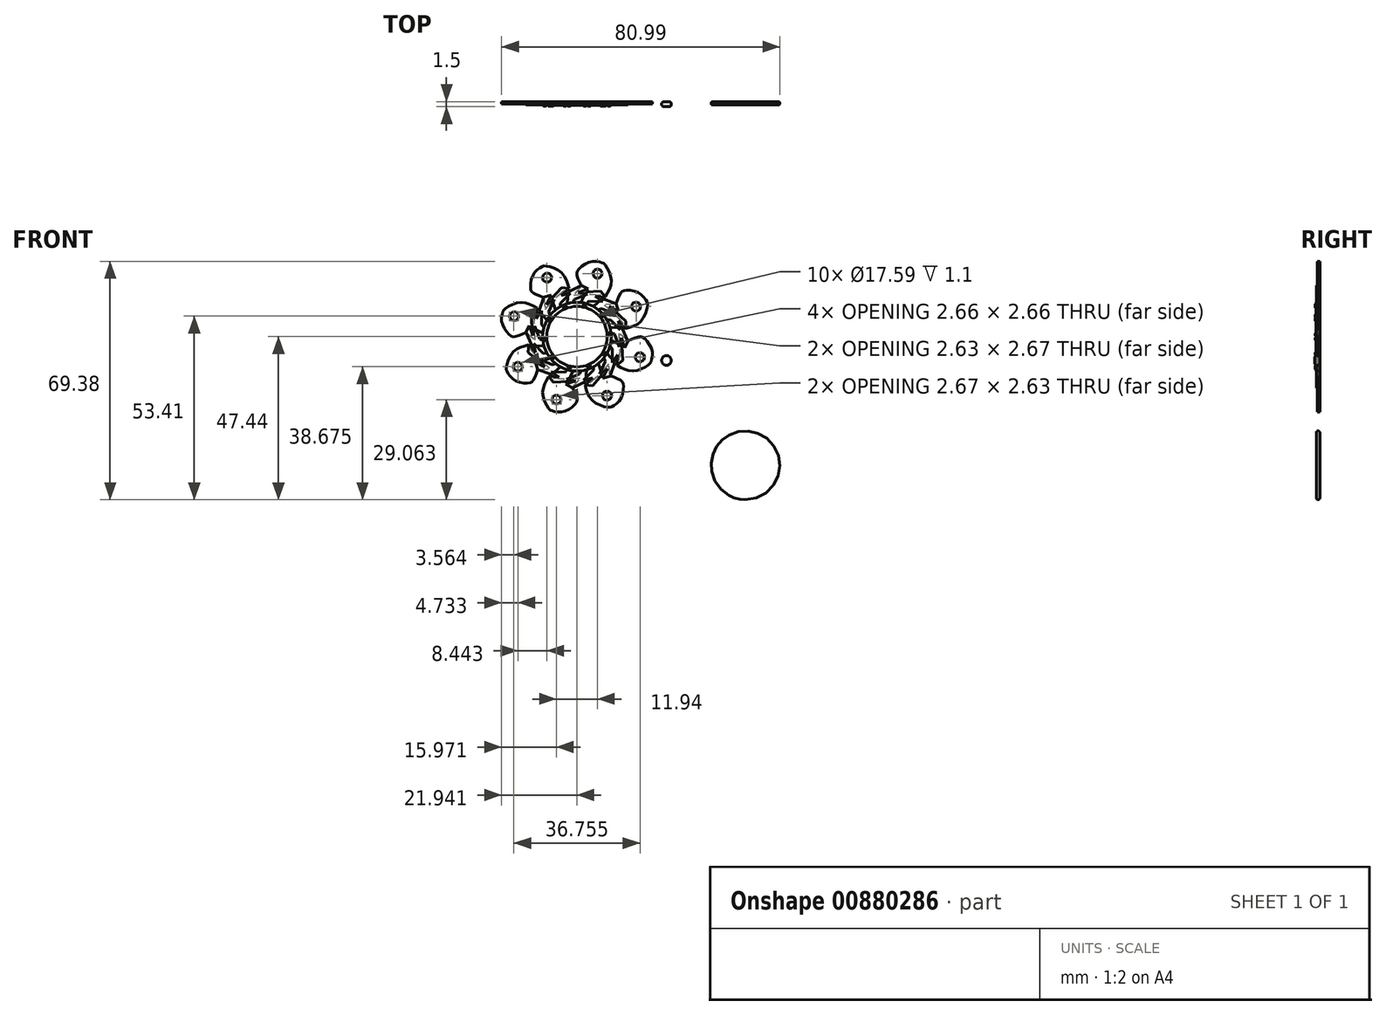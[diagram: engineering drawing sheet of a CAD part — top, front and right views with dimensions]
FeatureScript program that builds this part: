
annotation { "Feature Type Name" : "Feature", "Feature Type Description" : "" }
export const myFeature = defineFeature(function(context is Context, id is Id, definition is map)
    precondition{}
    {
        {
            var Q0;
            Q0=qCreatedBy(makeId("Front.planeOp"),FACE);
            var sketch = newSketch(context, id + "F0", { "sketchPlane" : qUnion([Q0])});
            skCircle(sketch, "E0", {"center": v(0, 0) * mm, "radius": 10 * mm});
            skSolve(sketch);
        }
        {
            var Q0;
            Q0=makeQuery(id+"F0.imprint","IMPRINT",FACE,{"disambiguationData":[TD([[makeQuery(id+"F0.imprint","IMPRINT",EDGE,{"derivedFrom":sQuery(id+"F0.wireOp",EDGE,"E0")}),1.0]])]});
            extrude(context, id + "F1", {"entities" : qUnion([Q0]), "depth" : 1 * mm, "offsetDistance" : 25 * mm});
        }
        {
            var Q0;
            Q0=makeQuery(id+"F1.opExtrude","CAP_FACE",FACE,{"disambiguationData":[OSD([sQuery(id+"F0.wireOp",EDGE,"E0")])],"isStart":false});
            var Q1;
            Q1=makeQuery(id+"F1.opExtrude","CAP_FACE",FACE,{"disambiguationData":[OSD([sQuery(id+"F0.wireOp",EDGE,"E0")])],"isStart":true});
            fillet(context, id + "F2", {"entities" : qUnion([Q0, Q1]), "radius" : .5 * mm, "tangentPropagation" : true, "allowEdgeOverflow" : false});
        }
        {
            var Q0;
            Q0=qCreatedBy(makeId("Front.planeOp"),FACE);
            var sketch = newSketch(context, id + "F3", { "sketchPlane" : qUnion([Q0])});
            skCircle(sketch, "E1", {"center": v(-49.05, 37.44) * mm, "radius": 10 * mm});
            skCircle(sketch, "E2", {"center": v(-49.05, 37.44) * mm, "radius": 8.8 * mm});
            skLineSegment(sketch, "E3", {"start": v(-53.96, 30.14) * mm, "end": v(-49.78, 31.59) * mm});
            skLineSegment(sketch, "E4", {"start": v(-49.78, 31.59) * mm, "end": v(-52.66, 29.42) * mm});
            skLineSegment(sketch, "E5", {"start": v(-44.68, 29.8) * mm, "end": v(-43.47, 33.75) * mm});
            skLineSegment(sketch, "E6", {"start": v(-43.47, 33.75) * mm, "end": v(-43.18, 30.9) * mm});
            skLineSegment(sketch, "E7", {"start": v(-40.26, 37.68) * mm, "end": v(-43.8, 39.95) * mm});
            skLineSegment(sketch, "E8", {"start": v(-43.8, 39.95) * mm, "end": v(-40.5, 39.5) * mm});
            skLineSegment(sketch, "E9", {"start": v(-44.85, 45.17) * mm, "end": v(-48.95, 42.78) * mm});
            skLineSegment(sketch, "E10", {"start": v(-48.95, 42.78) * mm, "end": v(-46.83, 45.95) * mm});
            skLineSegment(sketch, "E11", {"start": v(-53.1, 45.25) * mm, "end": v(-53.1, 40.62) * mm});
            skLineSegment(sketch, "E12", {"start": v(-53.1, 40.62) * mm, "end": v(-54.62, 44.24) * mm});
            skLineSegment(sketch, "E13", {"start": v(-57.81, 38.18) * mm, "end": v(-52.83, 35.52) * mm});
            skLineSegment(sketch, "E14", {"start": v(-52.83, 35.52) * mm, "end": v(-57.76, 36.22) * mm});
            skSolve(sketch);
        }
        {
            var Q0;
            Q0=makeQuery(id+"F3.imprint","IMPRINT",FACE,{"disambiguationData":[TD([[makeQuery(id+"F3.imprint","IMPRINT",EDGE,{"derivedFrom":sQuery(id+"F3.wireOp",EDGE,"E1")}),1.0]])]});
            extrude(context, id + "F4", {"entities" : qUnion([Q0]), "depth" : 1.1 * mm, "offsetDistance" : 25 * mm});
        }
        {
            var Q0;
            Q0=makeQuery(id+"F4.opExtrude","CAP_FACE",FACE,{"disambiguationData":[OSD([sQuery(id+"F3.wireOp",EDGE,"E1"),sQuery(id+"F3.wireOp",EDGE,"E2")])],"isStart":false});
            var sketch = newSketch(context, id + "F5", { "sketchPlane" : qUnion([Q0])});
            skCircle(sketch, "E15.cCircle", {"center": v(-58.44, 36.8) * mm, "radius": 0.45 * mm, "construction": true});
            skLineSegment(sketch, "E15.0", {"start": v(-58.13, 37.18) * mm, "end": v(-57.95, 36.78) * mm});
            skLineSegment(sketch, "E15.1", {"start": v(-57.95, 36.78) * mm, "end": v(-58.14, 36.4) * mm});
            skLineSegment(sketch, "E15.2", {"start": v(-58.14, 36.4) * mm, "end": v(-58.56, 36.31) * mm});
            skLineSegment(sketch, "E15.3", {"start": v(-58.56, 36.31) * mm, "end": v(-58.9, 36.59) * mm});
            skLineSegment(sketch, "E15.4", {"start": v(-58.9, 36.59) * mm, "end": v(-58.89, 37.02) * mm});
            skLineSegment(sketch, "E15.5", {"start": v(-58.89, 37.02) * mm, "end": v(-58.55, 37.28) * mm});
            skLineSegment(sketch, "E15.6", {"start": v(-58.55, 37.28) * mm, "end": v(-58.13, 37.18) * mm});
            skPoint(sketch, "E15.0.midPoint", {"position": v(-58.04, 36.98) * mm});
            skSolve(sketch);
        }
        {
            var Q0;
            Q0=makeQuery(id+"F5.imprint","IMPRINT",FACE,{"disambiguationData":[TD([[makeQuery(id+"F5.imprint","IMPRINT",EDGE,{"derivedFrom":sQuery(id+"F5.wireOp",EDGE,"E15.0")}),-1.0]])]});
            extrude(context, id + "F6", {"entities" : qUnion([Q0]), "operationType" : NewBodyOperationType.ADD, "depth" : .25 * mm, "offsetDistance" : 25 * mm, "hasSecondDirection" : true, "secondDirectionOppositeDirection" : true, "secondDirectionDepth" : .5 * mm});
        }
        {
            var Q0;
            Q0=makeQuery(id+"F6.opExtrude","CAP_FACE",FACE,{"disambiguationData":[OSD([sQuery(id+"F5.wireOp",EDGE,"E15.0"),sQuery(id+"F5.wireOp",EDGE,"E15.1"),sQuery(id+"F5.wireOp",EDGE,"E15.2"),sQuery(id+"F5.wireOp",EDGE,"E15.3"),sQuery(id+"F5.wireOp",EDGE,"E15.4"),sQuery(id+"F5.wireOp",EDGE,"E15.5"),sQuery(id+"F5.wireOp",EDGE,"E15.6")])],"isStart":false});
            fillet(context, id + "F7", {"entities" : qUnion([Q0]), "radius" : .3 * mm, "tangentPropagation" : true, "allowEdgeOverflow" : false});
        }
        {
            var Q0;
            Q0=makeQuery(id+"F4.opExtrude","SWEPT_BODY",BODY,{"disambiguationData":[OSD([sQuery(id+"F3.wireOp",EDGE,"E1"),sQuery(id+"F3.wireOp",EDGE,"E2")])]});
            var Q1;
            Q1=makeQuery(id+"F4.opExtrude","CAP_EDGE",EDGE,{"disambiguationData":[OSD([sQuery(id+"F3.wireOp",EDGE,"E2")])],"isStart":false});
            circularPattern(context, id + "F8", {"entities" : qUnion([Q0]), "axis" : qUnion([Q1]), "angle" : 360 * degree, "instanceCount" : 10, "equalSpace" : true});
        }
        {
            var Q0;
            Q0=qCreatedBy(makeId("Front.planeOp"),FACE);
            var sketch = newSketch(context, id + "F9", { "sketchPlane" : qUnion([Q0])});
            skLineSegment(sketch, "E16", {"start": v(-44.18, 46.23) * mm, "end": v(-41.66, 48.48) * mm});
            skLineSegment(sketch, "E17", {"start": v(-41.66, 48.48) * mm, "end": v(-37.6, 47.07) * mm});
            skLineSegment(sketch, "E18", {"start": v(-37.6, 47.07) * mm, "end": v(-36.95, 44.9) * mm});
            skLineSegment(sketch, "E19", {"start": v(-36.95, 44.9) * mm, "end": v(-39.69, 46.3) * mm});
            skLineSegment(sketch, "E20", {"start": v(-39.69, 46.3) * mm, "end": v(-38.15, 44.04) * mm});
            skLineSegment(sketch, "E21", {"start": v(-38.15, 44.04) * mm, "end": v(-41.9, 45.67) * mm});
            skLineSegment(sketch, "E22", {"start": v(-41.9, 45.67) * mm, "end": v(-42.8, 45.26) * mm});
            skLineSegment(sketch, "E23", {"start": v(-44.18, 46.23) * mm, "end": v(-42.8, 45.26) * mm});
            skSolve(sketch);
        }
        {
            var Q0;
            Q0=makeQuery(id+"F9.imprint","IMPRINT",FACE,{"disambiguationData":[TD([[makeQuery(id+"F9.imprint","IMPRINT",EDGE,{"derivedFrom":sQuery(id+"F9.wireOp",EDGE,"E16")}),-1.0]])]});
            extrude(context, id + "F10", {"entities" : qUnion([Q0]), "depth" : 1 * mm, "offsetDistance" : 25 * mm});
        }
        {
            var Q0;
            Q0=makeQuery(id+"F10.opExtrude","SWEPT_BODY",BODY,{"disambiguationData":[OSD([sQuery(id+"F9.wireOp",EDGE,"E16"),sQuery(id+"F9.wireOp",EDGE,"E17"),sQuery(id+"F9.wireOp",EDGE,"E18"),sQuery(id+"F9.wireOp",EDGE,"E19"),sQuery(id+"F9.wireOp",EDGE,"E20"),sQuery(id+"F9.wireOp",EDGE,"E21"),sQuery(id+"F9.wireOp",EDGE,"E22"),sQuery(id+"F9.wireOp",EDGE,"E23")])]});
            var Q1;
            Q1=makeQuery(id+"F8.opPattern","COPY",EDGE,{"derivedFrom":makeQuery(id+"F4.opExtrude","CAP_EDGE",EDGE,{"disambiguationData":[OSD([sQuery(id+"F3.wireOp",EDGE,"E2")])],"isStart":false}),"instanceName":"4"});
            circularPattern(context, id + "F11", {"entities" : qUnion([Q0]), "axis" : qUnion([Q1]), "angle" : 360 * degree, "instanceCount" : 16, "equalSpace" : true});
        }
        {
            var Q0;
            Q0=qCreatedBy(makeId("Front.planeOp"),FACE);
            var sketch = newSketch(context, id + "F12", { "sketchPlane" : qUnion([Q0])});
            skFitSpline(sketch, "E24", {"points": [v(-60.66, 45.73) * mm, v(-65.57, 47.4) * mm, v(-70.11, 45.48) * mm, v(-70.67, 44.55) * mm, v(-70.86, 41.37) * mm, v(-68.62, 37.9) * mm, v(-67.31, 37.4) * mm, v(-63.9, 38.7) * mm], "startDerivative": vector(-25.44, 14.89) * mm, "endDerivative": vector(25.26, 11.96) * mm});
            skLineSegment(sketch, "E25", {"start": v(-63.9, 38.7) * mm, "end": v(-61.22, 36.52) * mm});
            skLineSegment(sketch, "E26", {"start": v(-61.22, 36.52) * mm, "end": v(-61.45, 41.4) * mm});
            skLineSegment(sketch, "E27", {"start": v(-61.45, 41.4) * mm, "end": v(-61.17, 44.8) * mm});
            skLineSegment(sketch, "E28", {"start": v(-61.17, 44.8) * mm, "end": v(-60.66, 45.73) * mm});
            skSolve(sketch);
        }
        {
            var Q0;
            Q0=makeQuery(id+"F12.imprint","IMPRINT",FACE,{"disambiguationData":[TD([[makeQuery(id+"F12.imprint","IMPRINT",EDGE,{"derivedFrom":sQuery(id+"F12.wireOp",EDGE,"E24")}),1.0]])]});
            extrude(context, id + "F13", {"entities" : qUnion([Q0]), "depth" : .7 * mm, "offsetDistance" : 25 * mm});
        }
        {
            var Q0;
            Q0=makeQuery(id+"F13.opExtrude","CAP_FACE",FACE,{"disambiguationData":[OSD([sQuery(id+"F12.wireOp",EDGE,"E24"),sQuery(id+"F12.wireOp",EDGE,"E25"),sQuery(id+"F12.wireOp",EDGE,"E26"),sQuery(id+"F12.wireOp",EDGE,"E27"),sQuery(id+"F12.wireOp",EDGE,"E28")])],"isStart":false});
            var sketch = newSketch(context, id + "F14", { "sketchPlane" : qUnion([Q0])});
            skCircle(sketch, "E29.cCircle", {"center": v(-67.39, 43.41) * mm, "radius": 1.28 * mm, "construction": true});
            skLineSegment(sketch, "E29.0", {"start": v(-66.1, 43.87) * mm, "end": v(-66.1, 42.95) * mm});
            skLineSegment(sketch, "E29.1", {"start": v(-66.1, 42.95) * mm, "end": v(-66.7, 42.23) * mm});
            skLineSegment(sketch, "E29.2", {"start": v(-66.7, 42.23) * mm, "end": v(-67.62, 42.07) * mm});
            skLineSegment(sketch, "E29.3", {"start": v(-67.62, 42.07) * mm, "end": v(-68.43, 42.54) * mm});
            skLineSegment(sketch, "E29.4", {"start": v(-68.43, 42.54) * mm, "end": v(-68.74, 43.41) * mm});
            skLineSegment(sketch, "E29.5", {"start": v(-68.74, 43.41) * mm, "end": v(-68.43, 44.28) * mm});
            skLineSegment(sketch, "E29.6", {"start": v(-68.43, 44.28) * mm, "end": v(-67.62, 44.75) * mm});
            skLineSegment(sketch, "E29.7", {"start": v(-67.62, 44.75) * mm, "end": v(-66.7, 44.59) * mm});
            skLineSegment(sketch, "E29.8", {"start": v(-66.7, 44.59) * mm, "end": v(-66.1, 43.87) * mm});
            skPoint(sketch, "E29.0.midPoint", {"position": v(-66.1, 43.41) * mm});
            skSolve(sketch);
        }
        {
            var Q0;
            Q0=makeQuery(id+"F14.imprint","IMPRINT",FACE,{"disambiguationData":[TD([[makeQuery(id+"F14.imprint","IMPRINT",EDGE,{"derivedFrom":sQuery(id+"F14.wireOp",EDGE,"E29.0")}),-1.0]])]});
            extrude(context, id + "F15", {"entities" : qUnion([Q0]), "operationType" : NewBodyOperationType.REMOVE, "oppositeDirection" : true, "depth" : 25 * mm, "offsetDistance" : 25 * mm});
        }
        {
            var Q0;
            Q0=makeQuery(id+"F13.opExtrude","SWEPT_BODY",BODY,{"disambiguationData":[OSD([sQuery(id+"F12.wireOp",EDGE,"E24"),sQuery(id+"F12.wireOp",EDGE,"E25"),sQuery(id+"F12.wireOp",EDGE,"E26"),sQuery(id+"F12.wireOp",EDGE,"E27"),sQuery(id+"F12.wireOp",EDGE,"E28")])]});
            var Q1;
            Q1=makeQuery(id+"F4.opExtrude","CAP_EDGE",EDGE,{"disambiguationData":[OSD([sQuery(id+"F3.wireOp",EDGE,"E2")])],"isStart":false});
            circularPattern(context, id + "F16", {"entities" : qUnion([Q0]), "axis" : qUnion([Q1]), "angle" : 360 * degree, "instanceCount" : 8, "equalSpace" : true});
        }
        {
            var Q0;
            Q0=qCreatedBy(makeId("Front.planeOp"),FACE);
            var sketch = newSketch(context, id + "F17", { "sketchPlane" : qUnion([Q0])});
            skCircle(sketch, "E30", {"center": v(-23, 30.52) * mm, "radius": 1.41 * mm});
            skSolve(sketch);
        }
        {
            var Q0;
            Q0=makeQuery(id+"F17.imprint","IMPRINT",FACE,{"disambiguationData":[TD([[makeQuery(id+"F17.imprint","IMPRINT",EDGE,{"derivedFrom":sQuery(id+"F17.wireOp",EDGE,"E30")}),1.0]])]});
            var Q1;
            Q1=sQuery(id+"F17.wireOp",EDGE,"E30");
            extrude(context, id + "F18", {"entities" : qUnion([Q0]), "surfaceEntities" : qUnion([Q1]), "depth" : 1.5 * mm, "offsetDistance" : 25 * mm});
        }
        {
            var Q0;
            Q0=makeQuery(id+"F18.opExtrude","CAP_EDGE",EDGE,{"disambiguationData":[OSD([sQuery(id+"F17.wireOp",EDGE,"E30")])],"isStart":false});
            var Q1;
            Q1=makeQuery(id+"F18.opExtrude","SWEPT_FACE",FACE,{"disambiguationData":[OSD([sQuery(id+"F17.wireOp",EDGE,"E30")])]});
            var Q2;
            Q2=makeQuery(id+"F18.opExtrude","CAP_FACE",FACE,{"disambiguationData":[OSD([sQuery(id+"F17.wireOp",EDGE,"E30")])],"isStart":false});
            var Q3;
            Q3=makeQuery(id+"F18.opExtrude","CAP_FACE",FACE,{"disambiguationData":[OSD([sQuery(id+"F17.wireOp",EDGE,"E30")])],"isStart":true});
            var Q4;
            Q4=makeQuery(id+"F18.opExtrude","CAP_EDGE",EDGE,{"disambiguationData":[OSD([sQuery(id+"F17.wireOp",EDGE,"E30")])],"isStart":true});
            fillet(context, id + "F19", {"entities" : qUnion([Q0, Q1, Q2, Q3, Q4]), "radius" : .7 * mm, "tangentPropagation" : true, "allowEdgeOverflow" : false});
        }
    });
